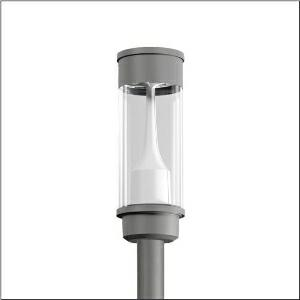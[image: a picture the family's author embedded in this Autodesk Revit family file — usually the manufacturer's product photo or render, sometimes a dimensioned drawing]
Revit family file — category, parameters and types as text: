
# Revit family: litepole_iq___p1_0a_5xa5415nf14h_8c95
name_source: partatom
category: Lighting Fixtures
units: mm (PartAtom-declared; Revit-internal decimal feet)

## family parameters
Cut with Voids When Loaded = No
Host = Face
Light Source = No
Part Type = Normal
Room Calculation Point = No
Round Connector Dimension = Use Diameter
Shared = No

## types (1)
- --- (1 x LED, 1510 lm, 11.8 W, 2700K)
    Apparent Load = 12 VA
    CIE Flux Codes = 32 61 90 93 100
    Color Rendering = 70
    Color Temperature = 2700K
    Default Elevation = 1800 mm
    Description = Litepole iQ, mast luminaire, Module 540 iQ-SR, primary light control with 3 zone facetted reflector, of plastic, silver coated, highly specular, structured, primary optical cover: cover, of PMMA, transparent, partly coated, light distribution: P1.0a, light emission: direct distribution, primary light characteristic: strongly asymmetric, installation type: post-top, LED, High Power LED, rated luminous flux: 1.510lm, luminous efficacy: 128lm/W, light colour: 727, colour temperature: 2700K, control gear: iQ Street-Remote, control: optimised constant luminous flux control (CLO 2.0), Desk-Remote (wireless, voltage-free reading and setting of iQ features in the workshop via application-optimized NFC function/RFID function), Light-Fading, Smart-Wire, Night-Set, Lumen-Switch, Temp-Guard, Auto-Match, Street-Remote, pre-setting: logarithmic dimming characteristic, with terminal, 6-pole, max. 2.5mm², mains connection: 230..240V, AC, 50/60Hz, start of lifetime: 12W, end of service life: 12W, reduction: 6W, luminaire housing, upper part, of glass-fibre reinforced polyester, coated, Siteco® metallic grey (DB 702S), diameter: 210mm, height: 590mm, spigot size: d x l = 76 x 70mm (post-top) | with reducer (optional accessory) 60 x 70mm, mounting height: 3..5m, post-top mast mounting element, of diecast aluminium, coated, Siteco® metallic grey (DB 702S), Module 540 iQ-SR, traffic white (RAL 9016), equipment: standard, protection rating (complete): IP65, insulation class (complete): insulation class II (safety insulation), certification: CE, ENEC, VDE, packaging unit: 1 piece

Light Distribution: P1.0a
    Height = 590 mm
    Lamp = 1 x LED
    Lamp Light Flux = 1510 lm
    Lamp Power = 11.8 W
    Lamp count = 1
    Length = 220 mm
    Luminous efficacy = 128 lm/W
    Manufacturer = Siteco
    ModVariant = No
    Model = 5XA5415NF14H
    Number of Poles = 1
    OnlyDefault = Yes
    Power Factor = 1
    Product Name = Litepole iQ | P1.0a
    Product group = mast luminaire | pylon top
    ProductGroupID = 6100
    Protection Class = Protection class II
    Protection Degree = IP 65
    RLX_Detail_Level = 1
    RLX_Emergency_Light_Flux = 0 lm
    RLX_Emergency_Type = 0
    RLX_Emergency_Type_DB = No
    RlxData = <blob elided: 63757 chars, md5=68f673fe>
    Socket = socket
    Standby Power = 0 W
    System Light Flux = 1510 lm
    System Power = 12 W
    Type Comments = factory setting: luminous flux: 100 % | dim-lin: 254 | 472 mA
    Type Image = l_1006025.jpg
    URL = http://relux.com
    VarID = @adj_152483
    Voltage = 0 V
    Weight = 0.00 kg
    Width = 0 mm  [stored 0 ft]

note: [stored X ft] marks values corroborated as IEEE doubles in the binary element streams (Revit-internal decimal feet)

## geometry (parser evidence)
native form markers: Blend x4, Sweep x11
no freeform markers — native parametric forms only
